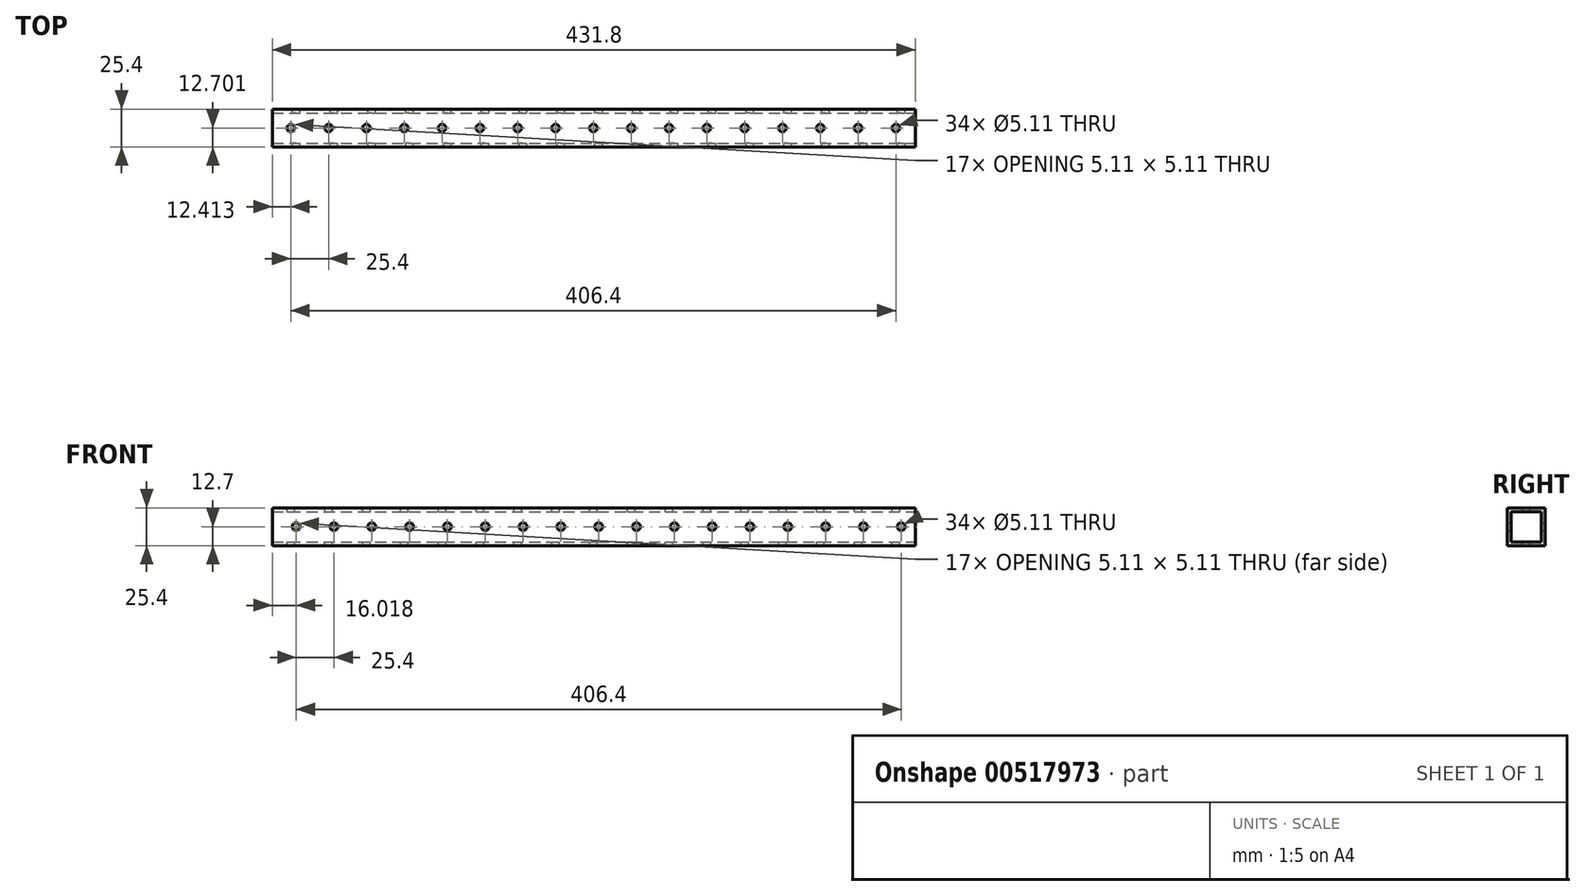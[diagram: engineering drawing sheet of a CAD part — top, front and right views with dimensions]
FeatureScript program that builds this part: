
annotation { "Feature Type Name" : "Feature", "Feature Type Description" : "" }
export const myFeature = defineFeature(function(context is Context, id is Id, definition is map)
    precondition{}
    {
        {
            var Q0;
            Q0=qCreatedBy(makeId("Top.planeOp"),FACE);
            var sketch = newSketch(context, id + "F0", { "sketchPlane" : qUnion([Q0])});
            skLineSegment(sketch, "E0.bottom", {"start": v(-218.5, -9.37) * mm, "end": v(213.3, -9.37) * mm});
            skLineSegment(sketch, "E0.top", {"start": v(-218.5, -34.77) * mm, "end": v(213.3, -34.77) * mm});
            skLineSegment(sketch, "E0.left", {"start": v(-218.5, -9.37) * mm, "end": v(-218.5, -34.77) * mm});
            skLineSegment(sketch, "E0.right", {"start": v(213.3, -9.37) * mm, "end": v(213.3, -34.77) * mm});
            skSolve(sketch);
        }
        {
            var Q0;
            Q0 = qSketchRegion(id + "F0", true);
            extrude(context, id + "F1", {"entities" : qUnion([Q0]), "depth" : 25.4 * mm, "offsetDistance" : 25.4 * mm});
        }
        {
            var Q0;
            Q0=makeQuery(id+"F1.opExtrude","SWEPT_FACE",FACE,{"disambiguationData":[OSD([sQuery(id+"F0.wireOp",EDGE,"E0.right")])]});
            var sketch = newSketch(context, id + "F2", { "sketchPlane" : qUnion([Q0])});
            skLineSegment(sketch, "E1.bottom", {"start": v(-32.23, 22.86) * mm, "end": v(-11.9, 22.86) * mm});
            skLineSegment(sketch, "E1.top", {"start": v(-32.23, 2.54) * mm, "end": v(-11.9, 2.54) * mm});
            skLineSegment(sketch, "E1.left", {"start": v(-32.23, 22.86) * mm, "end": v(-32.23, 2.54) * mm});
            skLineSegment(sketch, "E1.right", {"start": v(-11.9, 22.86) * mm, "end": v(-11.9, 2.54) * mm});
            skSolve(sketch);
        }
        {
            var Q0;
            Q0=makeQuery(id+"F2.imprint","IMPRINT",FACE,{"disambiguationData":[TD([[makeQuery(id+"F2.imprint","IMPRINT",EDGE,{"derivedFrom":sQuery(id+"F2.wireOp",EDGE,"E1.bottom")}),-1.0]])]});
            extrude(context, id + "F3", {"entities" : qUnion([Q0]), "operationType" : NewBodyOperationType.REMOVE, "oppositeDirection" : true, "depth" : 457.2 * mm, "offsetDistance" : 25.4 * mm});
        }
        {
            var Q0;
            Q0=makeQuery(id+"F1.opExtrude","CAP_FACE",FACE,{"disambiguationData":[OSD([sQuery(id+"F0.wireOp",EDGE,"E0.bottom"),sQuery(id+"F0.wireOp",EDGE,"E0.top"),sQuery(id+"F0.wireOp",EDGE,"E0.left"),sQuery(id+"F0.wireOp",EDGE,"E0.right")])],"isStart":false});
            var sketch = newSketch(context, id + "F4", { "sketchPlane" : qUnion([Q0])});
            skCircle(sketch, "E2", {"center": v(-206.09, -22.07) * mm, "radius": 2.55 * mm});
            skCircle(sketch, "E3.1.0.0", {"center": v(-180.69, -22.07) * mm, "radius": 2.55 * mm});
            skCircle(sketch, "E3.2.0.0", {"center": v(-155.29, -22.07) * mm, "radius": 2.55 * mm});
            skCircle(sketch, "E3.3.0.0", {"center": v(-129.89, -22.07) * mm, "radius": 2.55 * mm});
            skCircle(sketch, "E3.4.0.0", {"center": v(-104.49, -22.07) * mm, "radius": 2.55 * mm});
            skCircle(sketch, "E3.5.0.0", {"center": v(-79.09, -22.07) * mm, "radius": 2.55 * mm});
            skCircle(sketch, "E3.6.0.0", {"center": v(-53.69, -22.07) * mm, "radius": 2.55 * mm});
            skCircle(sketch, "E3.7.0.0", {"center": v(-28.29, -22.07) * mm, "radius": 2.55 * mm});
            skCircle(sketch, "E3.8.0.0", {"center": v(-2.89, -22.07) * mm, "radius": 2.55 * mm});
            skCircle(sketch, "E3.9.0.0", {"center": v(22.51, -22.07) * mm, "radius": 2.55 * mm});
            skCircle(sketch, "E3.10.0.0", {"center": v(47.91, -22.07) * mm, "radius": 2.55 * mm});
            skCircle(sketch, "E3.11.0.0", {"center": v(73.31, -22.07) * mm, "radius": 2.55 * mm});
            skCircle(sketch, "E3.12.0.0", {"center": v(98.71, -22.07) * mm, "radius": 2.55 * mm});
            skCircle(sketch, "E3.13.0.0", {"center": v(124.11, -22.07) * mm, "radius": 2.55 * mm});
            skCircle(sketch, "E3.14.0.0", {"center": v(149.51, -22.07) * mm, "radius": 2.55 * mm});
            skCircle(sketch, "E3.15.0.0", {"center": v(174.91, -22.07) * mm, "radius": 2.55 * mm});
            skCircle(sketch, "E3.16.0.0", {"center": v(200.31, -22.07) * mm, "radius": 2.55 * mm});
            skCircle(sketch, "E3.17.0.0", {"center": v(225.71, -22.07) * mm, "radius": 2.55 * mm});
            skLineSegment(sketch, "E3.direction1", {"start": v(-206.09, -22.07) * mm, "end": v(-180.69, -22.07) * mm, "construction": true});
            skSolve(sketch);
        }
        {
            var Q0;
            Q0=sQuery(id+"F4.wireOp",VERTEX,"E3.16.0.0.center");
            var Q1;
            Q1=sQuery(id+"F4.wireOp",VERTEX,"E3.14.0.0.center");
            var Q2;
            Q2=sQuery(id+"F4.wireOp",VERTEX,"E3.17.0.0.center");
            var Q3;
            Q3=sQuery(id+"F4.wireOp",VERTEX,"E3.11.0.0.center");
            var Q4;
            Q4=sQuery(id+"F4.wireOp",VERTEX,"E3.12.0.0.center");
            var Q5;
            Q5=sQuery(id+"F4.wireOp",VERTEX,"E3.13.0.0.center");
            var Q6;
            Q6=sQuery(id+"F4.wireOp",VERTEX,"E2.center");
            var Q7;
            Q7=sQuery(id+"F4.wireOp",VERTEX,"E3.1.0.0.center");
            var Q8;
            Q8=sQuery(id+"F4.wireOp",VERTEX,"E3.2.0.0.center");
            var Q9;
            Q9=sQuery(id+"F4.wireOp",VERTEX,"E3.3.0.0.center");
            var Q10;
            Q10=sQuery(id+"F4.wireOp",VERTEX,"E3.4.0.0.center");
            var Q11;
            Q11=sQuery(id+"F4.wireOp",VERTEX,"E3.5.0.0.center");
            var Q12;
            Q12=sQuery(id+"F4.wireOp",VERTEX,"E3.6.0.0.center");
            var Q13;
            Q13=sQuery(id+"F4.wireOp",VERTEX,"E3.15.0.0.center");
            var Q14;
            Q14=sQuery(id+"F4.wireOp",VERTEX,"E3.7.0.0.center");
            var Q15;
            Q15=sQuery(id+"F4.wireOp",VERTEX,"E3.8.0.0.center");
            var Q16;
            Q16=sQuery(id+"F4.wireOp",VERTEX,"E3.9.0.0.center");
            var Q17;
            Q17=sQuery(id+"F4.wireOp",VERTEX,"E3.10.0.0.center");
            var Q18;
            Q18=makeQuery(id+"F1.opExtrude","SWEPT_BODY",BODY,{"disambiguationData":[OSD([sQuery(id+"F0.wireOp",EDGE,"E0.bottom"),sQuery(id+"F0.wireOp",EDGE,"E0.top"),sQuery(id+"F0.wireOp",EDGE,"E0.left"),sQuery(id+"F0.wireOp",EDGE,"E0.right")])]});
            hole(context, id + "F5", {"style" : HoleStyle.SIMPLE, "endStyle" : HoleEndStyle.THROUGH, "holeDiameter" : 5.1 * mm, "isTappedThrough" : true, "tappedDepth" : 12.7 * mm, "tapClearance" : 3, "locations" : qUnion([Q0, Q1, Q2, Q3, Q4, Q5, Q6, Q7, Q8, Q9, Q10, Q11, Q12, Q13, Q14, Q15, Q16, Q17]), "scope" : qUnion([Q18])});
        }
        {
            var Q0;
            Q0=makeQuery(id+"F1.opExtrude","SWEPT_FACE",FACE,{"disambiguationData":[OSD([sQuery(id+"F0.wireOp",EDGE,"E0.bottom")])]});
            var sketch = newSketch(context, id + "F6", { "sketchPlane" : qUnion([Q0])});
            skCircle(sketch, "E4", {"center": v(-229.32, 12.7) * mm, "radius": 2.55 * mm});
            skCircle(sketch, "E5.1.0.0", {"center": v(-203.92, 12.7) * mm, "radius": 2.55 * mm});
            skCircle(sketch, "E5.2.0.0", {"center": v(-178.52, 12.7) * mm, "radius": 2.55 * mm});
            skCircle(sketch, "E5.3.0.0", {"center": v(-153.12, 12.7) * mm, "radius": 2.55 * mm});
            skCircle(sketch, "E5.4.0.0", {"center": v(-127.72, 12.7) * mm, "radius": 2.55 * mm});
            skCircle(sketch, "E5.5.0.0", {"center": v(-102.32, 12.7) * mm, "radius": 2.55 * mm});
            skCircle(sketch, "E5.6.0.0", {"center": v(-76.92, 12.7) * mm, "radius": 2.55 * mm});
            skCircle(sketch, "E5.7.0.0", {"center": v(-51.52, 12.7) * mm, "radius": 2.55 * mm});
            skCircle(sketch, "E5.8.0.0", {"center": v(-26.12, 12.7) * mm, "radius": 2.55 * mm});
            skCircle(sketch, "E5.9.0.0", {"center": v(-0.72, 12.7) * mm, "radius": 2.55 * mm});
            skCircle(sketch, "E5.10.0.0", {"center": v(24.68, 12.7) * mm, "radius": 2.55 * mm});
            skCircle(sketch, "E5.11.0.0", {"center": v(50.08, 12.7) * mm, "radius": 2.55 * mm});
            skCircle(sketch, "E5.12.0.0", {"center": v(75.48, 12.7) * mm, "radius": 2.55 * mm});
            skCircle(sketch, "E5.13.0.0", {"center": v(100.88, 12.7) * mm, "radius": 2.55 * mm});
            skCircle(sketch, "E5.14.0.0", {"center": v(126.28, 12.7) * mm, "radius": 2.55 * mm});
            skCircle(sketch, "E5.15.0.0", {"center": v(151.68, 12.7) * mm, "radius": 2.55 * mm});
            skCircle(sketch, "E5.16.0.0", {"center": v(177.08, 12.7) * mm, "radius": 2.55 * mm});
            skCircle(sketch, "E5.17.0.0", {"center": v(202.48, 12.7) * mm, "radius": 2.55 * mm});
            skLineSegment(sketch, "E5.direction1", {"start": v(-229.32, 12.7) * mm, "end": v(-203.92, 12.7) * mm, "construction": true});
            skSolve(sketch);
        }
        {
            var Q0;
            Q0=sQuery(id+"F6.wireOp",VERTEX,"E5.16.0.0.center");
            var Q1;
            Q1=sQuery(id+"F6.wireOp",VERTEX,"E5.15.0.0.center");
            var Q2;
            Q2=sQuery(id+"F6.wireOp",VERTEX,"E4.center");
            var Q3;
            Q3=sQuery(id+"F6.wireOp",VERTEX,"E5.2.0.0.center");
            var Q4;
            Q4=sQuery(id+"F6.wireOp",VERTEX,"E5.1.0.0.center");
            var Q5;
            Q5=sQuery(id+"F6.wireOp",VERTEX,"E5.4.0.0.center");
            var Q6;
            Q6=sQuery(id+"F6.wireOp",VERTEX,"E5.3.0.0.center");
            var Q7;
            Q7=sQuery(id+"F6.wireOp",VERTEX,"E5.11.0.0.center");
            var Q8;
            Q8=sQuery(id+"F6.wireOp",VERTEX,"E5.13.0.0.center");
            var Q9;
            Q9=sQuery(id+"F6.wireOp",VERTEX,"E5.12.0.0.center");
            var Q10;
            Q10=sQuery(id+"F6.wireOp",VERTEX,"E5.17.0.0.center");
            var Q11;
            Q11=sQuery(id+"F6.wireOp",VERTEX,"E5.14.0.0.center");
            var Q12;
            Q12=sQuery(id+"F6.wireOp",VERTEX,"E5.6.0.0.center");
            var Q13;
            Q13=sQuery(id+"F6.wireOp",VERTEX,"E5.5.0.0.center");
            var Q14;
            Q14=sQuery(id+"F6.wireOp",VERTEX,"E5.8.0.0.center");
            var Q15;
            Q15=sQuery(id+"F6.wireOp",VERTEX,"E5.7.0.0.center");
            var Q16;
            Q16=sQuery(id+"F6.wireOp",VERTEX,"E5.10.0.0.center");
            var Q17;
            Q17=sQuery(id+"F6.wireOp",VERTEX,"E5.9.0.0.center");
            var Q18;
            Q18=makeQuery(id+"F1.opExtrude","SWEPT_BODY",BODY,{"disambiguationData":[OSD([sQuery(id+"F0.wireOp",EDGE,"E0.bottom"),sQuery(id+"F0.wireOp",EDGE,"E0.top"),sQuery(id+"F0.wireOp",EDGE,"E0.left"),sQuery(id+"F0.wireOp",EDGE,"E0.right")])]});
            hole(context, id + "F7", {"style" : HoleStyle.SIMPLE, "endStyle" : HoleEndStyle.THROUGH, "holeDiameter" : 5.1 * mm, "isTappedThrough" : true, "tappedDepth" : 12.7 * mm, "tapClearance" : 3, "locations" : qUnion([Q0, Q1, Q2, Q3, Q4, Q5, Q6, Q7, Q8, Q9, Q10, Q11, Q12, Q13, Q14, Q15, Q16, Q17]), "scope" : qUnion([Q18])});
        }
    });
